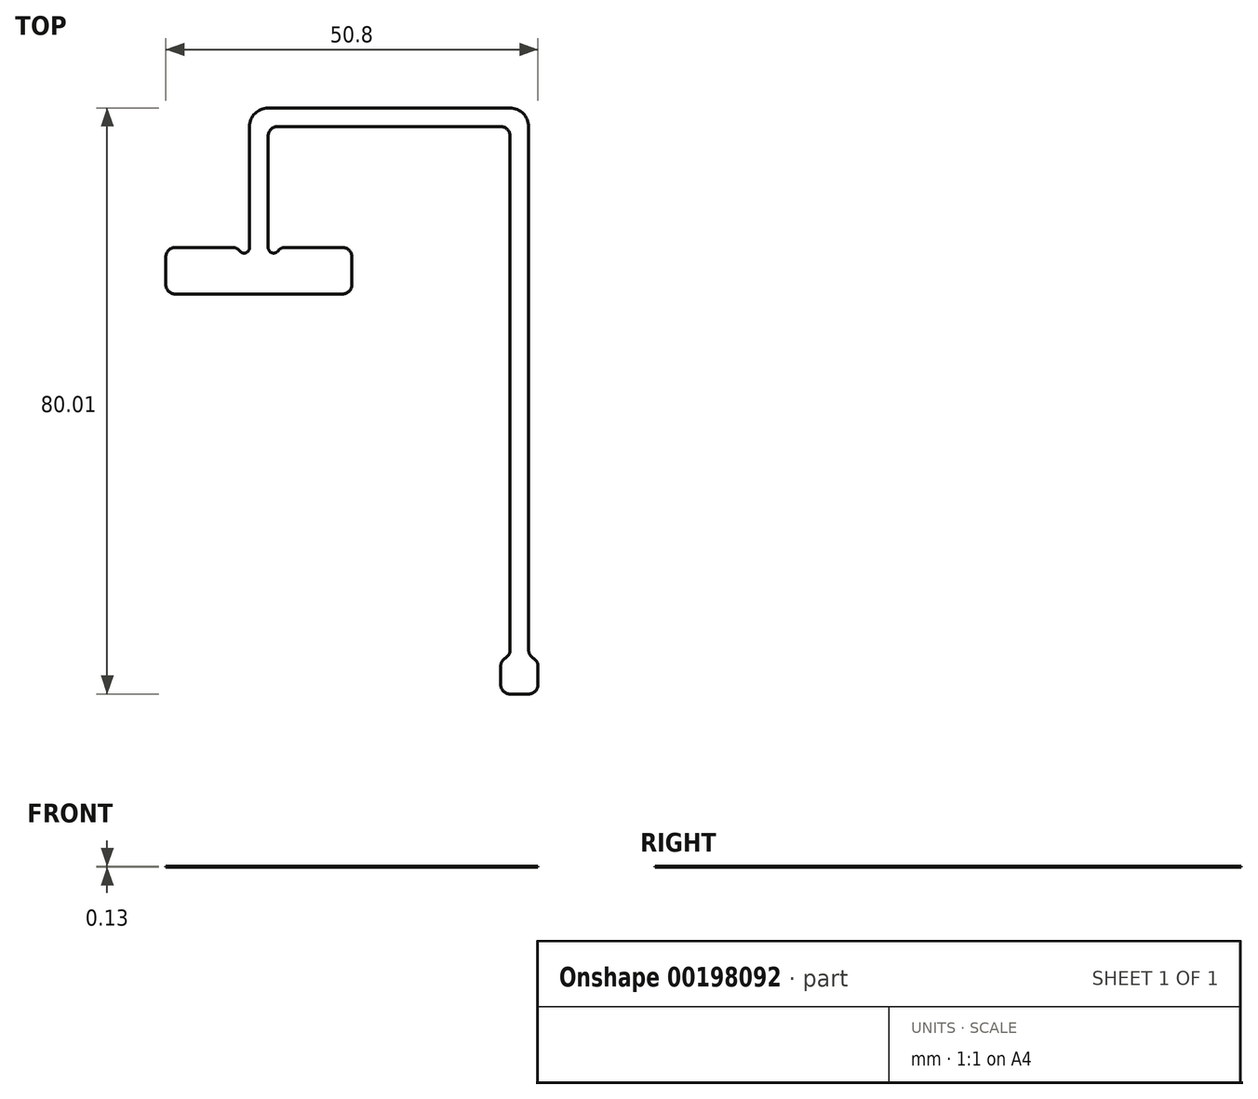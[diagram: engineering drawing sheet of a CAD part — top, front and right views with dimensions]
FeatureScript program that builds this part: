
annotation { "Feature Type Name" : "Feature", "Feature Type Description" : "" }
export const myFeature = defineFeature(function(context is Context, id is Id, definition is map)
    precondition{}
    {
        {
            var Q0;
            Q0=qCreatedBy(makeId("Top.planeOp"),FACE);
            var sketch = newSketch(context, id + "F0", { "sketchPlane" : qUnion([Q0])});
            skLineSegment(sketch, "E0.bottom", {"start": v(1.27, 0) * mm, "end": v(24.13, 0) * mm});
            skLineSegment(sketch, "E0.top", {"start": v(1.27, 6.35) * mm, "end": v(9.2, 6.35) * mm});
            skLineSegment(sketch, "E0.left", {"start": v(0, 1.27) * mm, "end": v(0, 5.08) * mm});
            skLineSegment(sketch, "E0.right", {"start": v(25.4, 1.27) * mm, "end": v(25.4, 5.08) * mm});
            skPoint(sketch, "E1.visualSharp", {"position": v(0, 6.35) * mm});
            skArc(sketch, "E1.filletArc", {"start": v(1.27, 6.35) * mm, "mid": v(0.37, 5.98) * mm, "end": v(0, 5.08) * mm});
            skPoint(sketch, "E2.visualSharp", {"position": v(0, 0) * mm});
            skArc(sketch, "E2.filletArc", {"start": v(0, 1.27) * mm, "mid": v(0.37, 0.37) * mm, "end": v(1.27, 0) * mm});
            skPoint(sketch, "E3.visualSharp", {"position": v(25.4, 6.35) * mm});
            skArc(sketch, "E3.filletArc", {"start": v(25.4, 5.08) * mm, "mid": v(25.03, 5.98) * mm, "end": v(24.13, 6.35) * mm});
            skPoint(sketch, "E4.visualSharp", {"position": v(25.4, 0) * mm});
            skArc(sketch, "E4.filletArc", {"start": v(24.13, 0) * mm, "mid": v(25.03, 0.37) * mm, "end": v(25.4, 1.27) * mm});
            skLineSegment(sketch, "E5", {"start": v(12.7, 6.35) * mm, "end": v(12.7, 24.13) * mm, "construction": true});
            skLineSegment(sketch, "E6", {"start": v(12.7, 24.13) * mm, "end": v(48.26, 24.13) * mm, "construction": true});
            skLineSegment(sketch, "E7", {"start": v(48.26, 24.13) * mm, "end": v(48.26, -52.07) * mm, "construction": true});
            skLineSegment(sketch, "E8.bottom", {"start": v(49.53, -54.61) * mm, "end": v(47, -54.61) * mm});
            skLineSegment(sketch, "E8.top", {"start": v(49.53, -49.53) * mm, "end": v(47, -49.53) * mm, "construction": true});
            skLineSegment(sketch, "E8.left", {"start": v(50.8, -53.34) * mm, "end": v(50.8, -50.8) * mm});
            skLineSegment(sketch, "E8.right", {"start": v(45.72, -53.34) * mm, "end": v(45.72, -50.8) * mm});
            skPoint(sketch, "E8.middle", {"position": v(48.26, -52.07) * mm});
            skLineSegment(sketch, "E9.0", {"start": v(13.97, 6.35) * mm, "end": v(13.97, 21.59) * mm});
            skLineSegment(sketch, "E10.0", {"start": v(11.43, 6.35) * mm, "end": v(11.43, 22.86) * mm});
            skLineSegment(sketch, "E11.0", {"start": v(15.24, 22.86) * mm, "end": v(45.72, 22.86) * mm});
            skLineSegment(sketch, "E12.0", {"start": v(13.97, 25.4) * mm, "end": v(46.99, 25.4) * mm});
            skLineSegment(sketch, "E13.0", {"start": v(46.99, 21.59) * mm, "end": v(47, -48.6) * mm});
            skLineSegment(sketch, "E14.0", {"start": v(49.53, 22.86) * mm, "end": v(49.53, -48.6) * mm});
            skPoint(sketch, "E15.visualSharp", {"position": v(11.43, 25.4) * mm});
            skArc(sketch, "E15.filletArc", {"start": v(13.97, 25.4) * mm, "mid": v(12.17, 24.66) * mm, "end": v(11.43, 22.86) * mm});
            skArc(sketch, "E16.filletArc", {"start": v(15.24, 22.86) * mm, "mid": v(14.34, 22.49) * mm, "end": v(13.97, 21.59) * mm});
            skPoint(sketch, "E17.visualSharp", {"position": v(46.99, 22.86) * mm});
            skArc(sketch, "E17.filletArc", {"start": v(46.99, 21.59) * mm, "mid": v(46.62, 22.49) * mm, "end": v(45.72, 22.86) * mm});
            skPoint(sketch, "E18.visualSharp", {"position": v(49.53, 25.4) * mm});
            skArc(sketch, "E18.filletArc", {"start": v(49.53, 22.86) * mm, "mid": v(48.79, 24.66) * mm, "end": v(46.99, 25.4) * mm});
            skPoint(sketch, "E19.visualSharp", {"position": v(45.72, -49.53) * mm});
            skArc(sketch, "E19.filletArc", {"start": v(46.36, -49.7) * mm, "mid": v(45.9, -50.16) * mm, "end": v(45.72, -50.8) * mm});
            skPoint(sketch, "E20.visualSharp", {"position": v(50.8, -49.53) * mm});
            skArc(sketch, "E20.filletArc", {"start": v(50.8, -50.8) * mm, "mid": v(50.63, -50.16) * mm, "end": v(50.17, -49.7) * mm});
            skPoint(sketch, "E21.visualSharp", {"position": v(45.72, -54.61) * mm});
            skArc(sketch, "E21.filletArc", {"start": v(45.72, -53.34) * mm, "mid": v(46.1, -54.24) * mm, "end": v(47, -54.61) * mm});
            skPoint(sketch, "E22.visualSharp", {"position": v(50.8, -54.61) * mm});
            skArc(sketch, "E22.filletArc", {"start": v(49.53, -54.61) * mm, "mid": v(50.43, -54.24) * mm, "end": v(50.8, -53.34) * mm});
            skArc(sketch, "E23.filletArc", {"start": v(46.36, -49.7) * mm, "mid": v(46.82, -49.24) * mm, "end": v(47, -48.6) * mm});
            skArc(sketch, "E24.filletArc", {"start": v(49.53, -48.6) * mm, "mid": v(49.7, -49.24) * mm, "end": v(50.17, -49.7) * mm});
            skArc(sketch, "E25", {"start": v(10.04, 5.91) * mm, "mid": v(10.9, 5.62) * mm, "end": v(11.43, 6.35) * mm});
            skPoint(sketch, "E26.visualSharp", {"position": v(9.9, 6.35) * mm});
            skArc(sketch, "E26.filletArc", {"start": v(10.04, 5.91) * mm, "mid": v(9.68, 6.23) * mm, "end": v(9.2, 6.35) * mm});
            skArc(sketch, "E27", {"start": v(13.97, 6.35) * mm, "mid": v(14.5, 5.62) * mm, "end": v(15.36, 5.91) * mm});
            skLineSegment(sketch, "E28.trimOffspring", {"start": v(16.2, 6.35) * mm, "end": v(24.13, 6.35) * mm});
            skPoint(sketch, "E29.visualSharp", {"position": v(15.5, 6.35) * mm});
            skArc(sketch, "E29.filletArc", {"start": v(16.2, 6.35) * mm, "mid": v(15.72, 6.23) * mm, "end": v(15.36, 5.91) * mm});
            skLineSegment(sketch, "E30", {"start": v(10.67, 6.35) * mm, "end": v(14.73, 6.35) * mm, "construction": true});
            skSolve(sketch);
        }
        {
            var Q0;
            Q0 = qSketchRegion(id + "F0", true);
            extrude(context, id + "F1", {"entities" : qUnion([Q0]), "depth" : 0.13 * mm});
        }
    });
